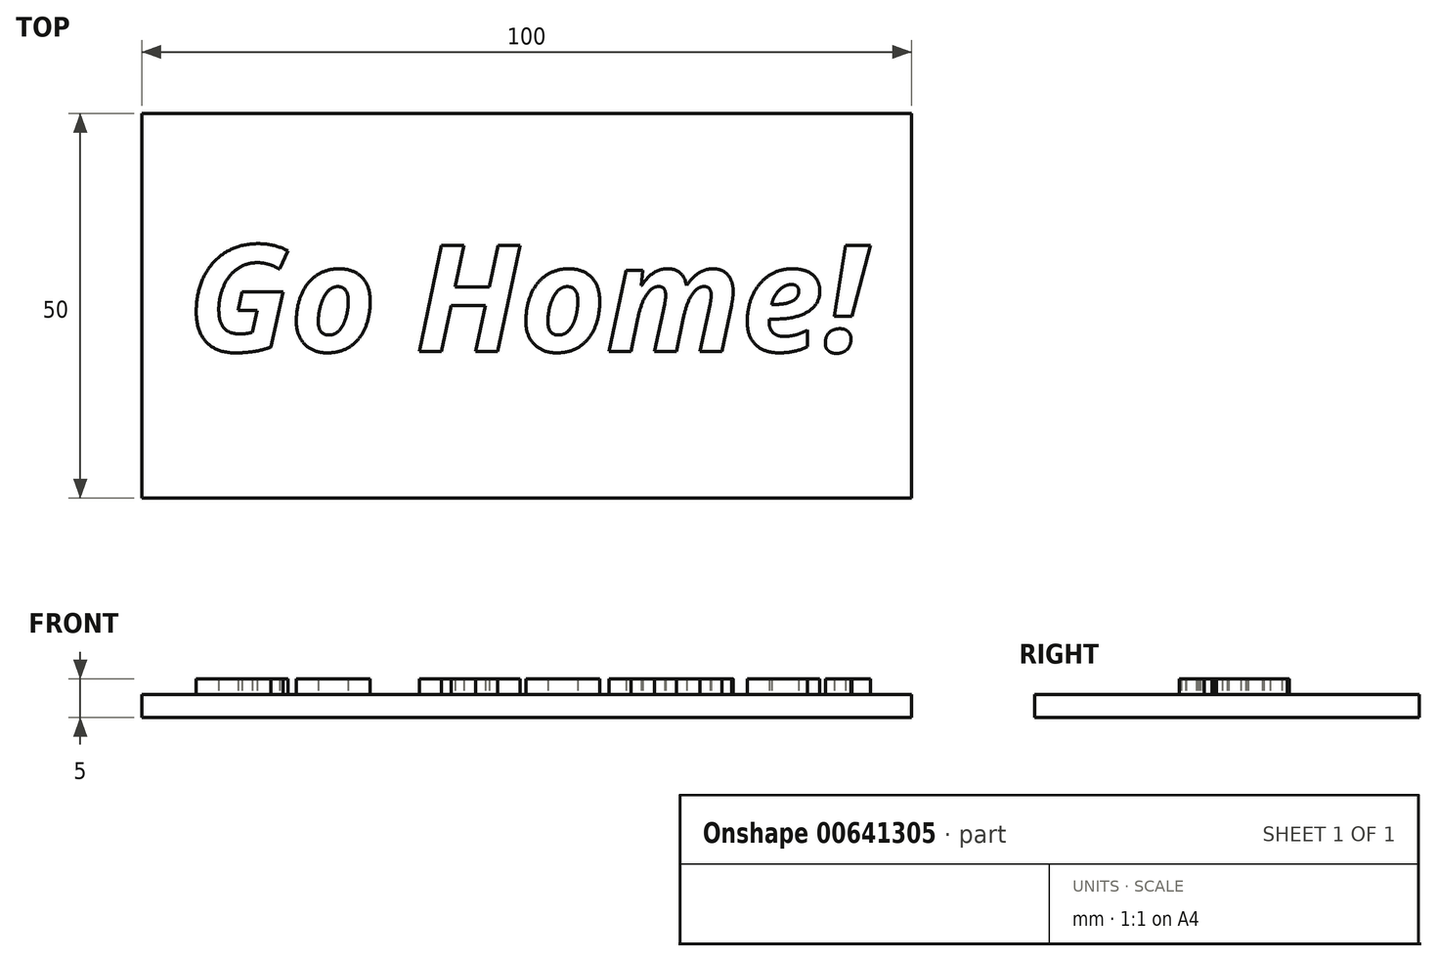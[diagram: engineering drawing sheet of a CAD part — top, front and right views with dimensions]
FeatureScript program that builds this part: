
annotation { "Feature Type Name" : "Feature", "Feature Type Description" : "" }
export const myFeature = defineFeature(function(context is Context, id is Id, definition is map)
    precondition{}
    {
        {
            var Q0;
            Q0=qCreatedBy(makeId("Top.planeOp"),FACE);
            var sketch = newSketch(context, id + "F0", { "sketchPlane" : qUnion([Q0])});
            skLineSegment(sketch, "E0.bottom", {"start": v(0, 0) * mm, "end": v(-100, 0) * mm});
            skLineSegment(sketch, "E0.top", {"start": v(0, 50) * mm, "end": v(-100, 50) * mm});
            skLineSegment(sketch, "E0.left", {"start": v(0, 0) * mm, "end": v(0, 50) * mm});
            skLineSegment(sketch, "E0.right", {"start": v(-100, 0) * mm, "end": v(-100, 50) * mm});
            skSolve(sketch);
        }
        {
            var Q0;
            Q0=makeQuery(id+"F0.imprint","IMPRINT",FACE,{"disambiguationData":[TD([[makeQuery(id+"F0.imprint","IMPRINT",EDGE,{"derivedFrom":sQuery(id+"F0.wireOp",EDGE,"E0.bottom")}),-1.0]])]});
            extrude(context, id + "F1", {"entities" : qUnion([Q0]), "depth" : 3 * mm, "offsetDistance" : 25 * mm});
        }
        {
            var Q0;
            Q0=makeQuery(id+"F1.opExtrude","CAP_FACE",FACE,{"disambiguationData":[OSD([sQuery(id+"F0.wireOp",EDGE,"E0.bottom"),sQuery(id+"F0.wireOp",EDGE,"E0.top"),sQuery(id+"F0.wireOp",EDGE,"E0.left"),sQuery(id+"F0.wireOp",EDGE,"E0.right")])],"isStart":false});
            var sketch = newSketch(context, id + "F2", { "sketchPlane" : qUnion([Q0])});
            skText(sketch, "E1", { "text": "Go Home!", "fontName": "OpenSans-BoldItalic.ttf"});
            const initialGuessF2  = {"E1": [-0.0941, 0.01907, 1, 0, 0.0139]};
            skSetInitialGuess(sketch, initialGuessF2);
            skSolve(sketch);
        }
        {
            var Q0;
            Q0 = qSketchRegion(id + "F2", true);
            extrude(context, id + "F3", {"entities" : qUnion([Q0]), "operationType" : NewBodyOperationType.ADD, "depth" : 2 * mm, "offsetDistance" : 25 * mm});
        }
    });
